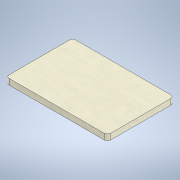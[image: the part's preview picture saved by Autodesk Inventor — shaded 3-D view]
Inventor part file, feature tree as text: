
AUTODESK INVENTOR PART (.ipt)
format: ipt  version: 2021 (Build 250183000, 183)  size: 115,200 bytes
history: native  units: mm
features: extrude x1, sketch x1
ambient origin geometry x8: Origin, YZ Plane, XZ Plane, XY Plane, X Axis, Y Axis, Z Axis, Center Point
bodies: Solid1 (feature_tree)
feature tree (2):
  extrude  "Extrusion1"  Depth=42.0mm
  sketch  "Sketch1"  dims[d0=64.0mm d1=42.0mm d2=2.0mm d3=3.7mm d4=0.0mm]
